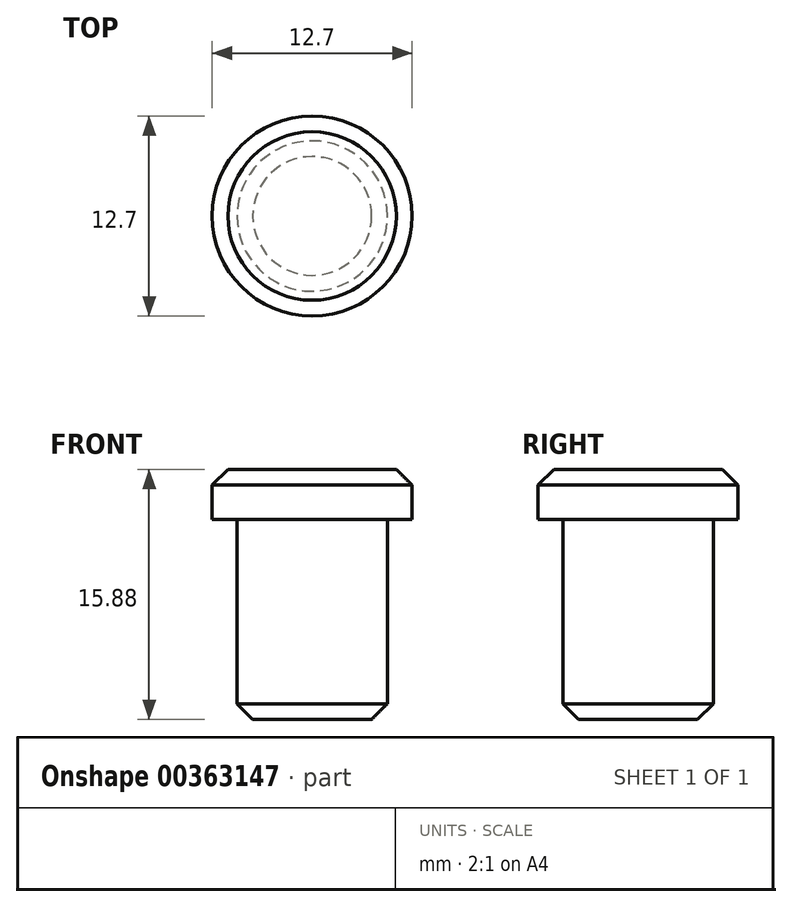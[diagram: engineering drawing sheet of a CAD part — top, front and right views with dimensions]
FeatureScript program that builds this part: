
annotation { "Feature Type Name" : "Feature", "Feature Type Description" : "" }
export const myFeature = defineFeature(function(context is Context, id is Id, definition is map)
    precondition{}
    {
        {
            var Q0;
            Q0=qCreatedBy(makeId("Front.planeOp"),FACE);
            var sketch = newSketch(context, id + "F0", { "sketchPlane" : qUnion([Q0])});
            skLineSegment(sketch, "E0.top", {"start": v(0, -15.88) * mm, "end": v(4.78, -15.88) * mm});
            skLineSegment(sketch, "E0.left", {"start": v(0, 0) * mm, "end": v(0, -15.88) * mm});
            skLineSegment(sketch, "E0.right", {"start": v(4.78, -3.18) * mm, "end": v(4.78, -15.88) * mm});
            skLineSegment(sketch, "E1", {"start": v(0, 0) * mm, "end": v(6.35, 0) * mm});
            skLineSegment(sketch, "E2", {"start": v(6.35, 0) * mm, "end": v(6.35, -3.18) * mm});
            skLineSegment(sketch, "E3", {"start": v(6.35, -3.18) * mm, "end": v(4.78, -3.18) * mm});
            skSolve(sketch);
        }
        {
            var Q0;
            Q0=qSketchRegion(id+"F0",true);
            var Q1;
            Q1=sQuery(id+"F0.wireOp",EDGE,"E0.left");
            revolve(context, id + "F1", {"entities" : qUnion([Q0]), "axis" : qUnion([Q1]), "revolveType" : RevolveType.FULL});
        }
        {
            var Q0;
            Q0=makeQuery(id+"F1.opRevolve","SWEPT_EDGE",EDGE,{"disambiguationData":[OSD([sQuery(id+"F0.wireOp",EDGE,"E1"),sQuery(id+"F0.wireOp",EDGE,"E2")])]});
            var Q1;
            Q1=makeQuery(id+"F1.opRevolve","SWEPT_EDGE",EDGE,{"disambiguationData":[OSD([sQuery(id+"F0.wireOp",EDGE,"E0.top"),sQuery(id+"F0.wireOp",EDGE,"E0.right")])]});
            chamfer(context, id + "F2", {"entities" : qUnion([Q0, Q1]), "width" : 1 * mm, "tangentPropagation" : true});
        }
    });
